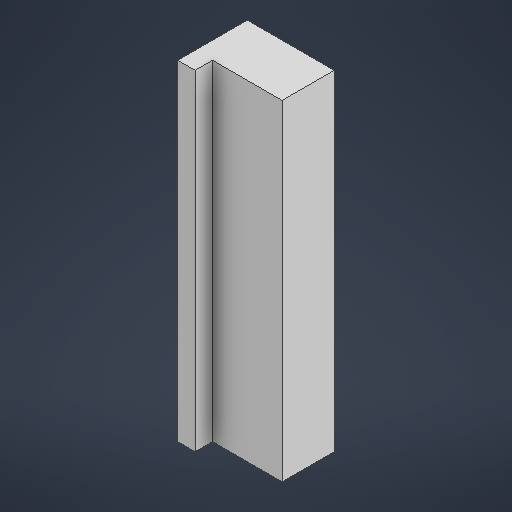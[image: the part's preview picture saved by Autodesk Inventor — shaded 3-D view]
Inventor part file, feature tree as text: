
AUTODESK INVENTOR PART (.ipt)
format: ipt  version: 2025 (Build 290162000, 162)  size: 185,856 bytes
history: native  units: mm
features: extrude x2, sketch x2
ambient origin geometry x8: Origin, YZ Plane, XZ Plane, XY Plane, X Axis, Y Axis, Z Axis, Center Point
bodies: 实体1 (feature_tree)
feature tree (4):
  extrude  "拉伸1"  Depth=19.0mm
  extrude  "拉伸2"  Depth=1.0mm
  sketch  "草图1"  dims[d0=5.0mm d1=19.0mm]
  sketch  "草图2"  dims[d2=3.0mm d3=0.0mm d4=1.0mm d5=1.0mm d6=0.0mm]
